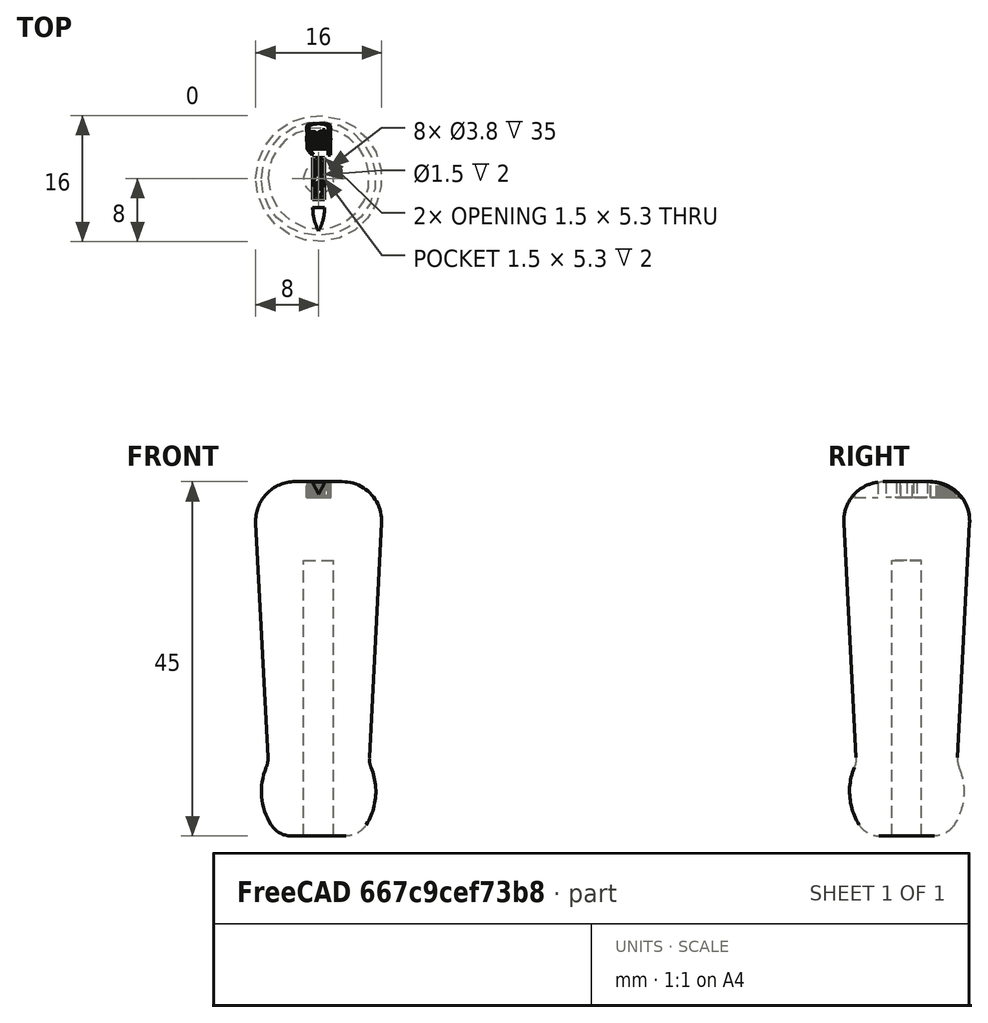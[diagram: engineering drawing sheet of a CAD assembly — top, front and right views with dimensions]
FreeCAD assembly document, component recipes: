
FREECAD ASSEMBLY — COMPONENT RECIPES ("NeedleFileHandle")

This assembly document has 10 components, labeled P0..P9 below (a component is one placed body or linked part). 10 of them carry a construction recipe — the FreeCAD feature program that regenerates the part from scratch, quoted from this document or its linked companion documents; the rest are supplied as boundary geometry only. No exploded tour is included for this assembly.
COMPONENT P0 — recipe-attached ("3 - Dagger Rounded", modeled in this document).
Construction recipe (the document's own serialized feature program — sketch geometry with constraints, then the solid features built on it; lengths are millimeters unless a unit is written):

FEATURE [Sketcher::SketchObject] Sketch004
  ArcFitTolerance = 1e-06
  AttachmentSupport = -> [XZ_Plane005]
  FullyConstrained = true
  MakeInternals = false
  MapMode = 5
  Placement = pos=(0,0,0) rot=(1,0,0;1.5708rad)
  expr: Constraints[10] = <<Spreadsheet>>.TopFlatDiameter / 2
  expr: Constraints[22] = <<Spreadsheet>>.TopRadius
  expr: Constraints[23] = <<Spreadsheet>>.BottomRadius1
  expr: Constraints[24] = <<Spreadsheet>>.BottomRadius2
  expr: Constraints[25] = <<Spreadsheet>>.BottomToStraightHeight
  expr: Constraints[26] = <<Spreadsheet>>.BottomFlatDiameter / 2
  expr: Constraints[27] = <<Spreadsheet>>.BottomRadius3
  expr: Constraints[5] = <<Spreadsheet>>.HoleDiameter / 2
  expr: Constraints[6] = <<Spreadsheet>>.HoleDepth
  expr: Constraints[7] = <<Spreadsheet>>.TopSolidLength
  sketch-geometry (10):
    g0: LineSegment StartX=-1.9 StartY=0 StartZ=0 EndX=-1.9 EndY=35 EndZ=0
    g1: LineSegment StartX=-1.9 StartY=35 StartZ=0 EndX=0 EndY=35 EndZ=0
    g2: LineSegment StartX=0 StartY=35 StartZ=0 EndX=0 EndY=45 EndZ=0
    g3: LineSegment StartX=0 StartY=45 StartZ=0 EndX=-3 EndY=45 EndZ=0
    g4: ArcOfCircle CenterX=-3 CenterY=40 CenterZ=0 NormalX=0 NormalY=0 NormalZ=1 AngleXU=0 Radius=5 StartAngle=1.5708 EndAngle=3.19395
    g5: LineSegment StartX=-1.9 StartY=0 StartZ=0 EndX=-3.5 EndY=0 EndZ=0
    g6: ArcOfCircle CenterX=-3.5 CenterY=3 CenterZ=0 NormalX=0 NormalY=0 NormalZ=1 AngleXU=0 Radius=3 StartAngle=3.70042 EndAngle=4.71239
    g7: ArcOfCircle CenterX=0.739385 CenterY=5.65096 CenterZ=0 NormalX=0 NormalY=0 NormalZ=1 AngleXU=0 Radius=8 StartAngle=2.75061 EndAngle=3.70042
    g8: ArcOfCircle CenterX=-9.43052 CenterY=9.84299 CenterZ=0 NormalX=0 NormalY=0 NormalZ=1 AngleXU=0 Radius=3 StartAngle=5.89221 EndAngle=6.33555
    g9: LineSegment StartX=-6.43463 StartY=10 StartZ=0 EndX=-7.99315 EndY=39.7383 EndZ=0
  constraints (28):
    c: PointOnObject(g0,g-1)
    c: Vertical(g0)
    c: Coincident(g0,g1)
    c: PointOnObject(g1,g-2)
    c: Horizontal(g1)
    c: DistanceX(g1,g1) = 1.9
    c: DistanceY(g0,g0) = 35
    c: Distance(g2) = 10
    c: Coincident(g2,g1)
    c: PointOnObject(g2,g-2)
    c: Distance(g3) = 3
    c: Coincident(g3,g2)
    c: Horizontal(g3)
    c: Coincident(g5,g0)
    c: PointOnObject(g5,g-1)
    c: Tangent(g6,g5) = 1.5708
    c: Tangent(g7,g6) = -1.5708
    c: Tangent(g8,g7) = 1.5708
    c: Tangent(g9,g8) = -1.5708
    c: Tangent(g4,g3) = -1.5708
    c: Tangent(g9,g4) = 1.5708
    c: Angle(g-2,g9) = 0.0523599
    c: Radius(g4) = 5
    c: Radius(g6) = 3
    c: Radius(g7) = 8
    c: DistanceY(g8) = 10
    c: DistanceX(g5,g-1) = 3.5
    c: Radius(g8) = 3
FEATURE [PartDesign::Revolution] Revolution002
  Angle = 360
  Angle2 = 60
  Axis = (0,2e-16,1)
  Base = (0,0,0)
  Placement = pos=(0,0,0) rot=(1,0,0;1.5708rad)
  Profile = -> Sketch004
  ReferenceAxis = -> Sketch004 [V_Axis]
  Refine = true
  Suppressed = false
  Type = 0
FEATURE [Sketcher::SketchObject] Sketch005
  ArcFitTolerance = 1e-06
  AttachmentSupport = -> [Revolution002]
  FullyConstrained = true
  MakeInternals = false
  MapMode = 5
  Placement = pos=(0,1e-14,45) rot=(0,0,1;3.14159rad)
  sketch-geometry (11):
    g0: LineSegment [constr] StartX=-0.75 StartY=-2.65 StartZ=0 EndX=0.75 EndY=-2.65 EndZ=0
    g1: LineSegment [constr] StartX=0.75 StartY=-2.65 StartZ=0 EndX=0.75 EndY=2.65 EndZ=0
    g2: LineSegment [constr] StartX=0.75 StartY=2.65 StartZ=0 EndX=-0.75 EndY=2.65 EndZ=0
    g3: LineSegment [constr] StartX=-0.75 StartY=2.65 StartZ=0 EndX=-0.75 EndY=-2.65 EndZ=0
    g4: GeomPoint [constr] X=0 Y=0 Z=0
    g5: LineSegment StartX=-0.75 StartY=3.65 StartZ=0 EndX=0.75 EndY=3.65 EndZ=0
    g6: ArcOfCircle CenterX=5.625 CenterY=3.65 CenterZ=0 NormalX=0 NormalY=0 NormalZ=1 AngleXU=0 Radius=6.375 StartAngle=2.65164 EndAngle=3.14159
    g7: ArcOfCircle CenterX=-5.625 CenterY=3.65 CenterZ=0 NormalX=0 NormalY=0 NormalZ=1 AngleXU=0 Radius=6.375 StartAngle=0 EndAngle=0.489957
    g8: ArcOfCircle CenterX=4.30667 CenterY=-7e-16 CenterZ=0 NormalX=0 NormalY=0 NormalZ=1 AngleXU=0 Radius=5.05667 StartAngle=2.58998 EndAngle=3.6932
    g9: ArcOfCircle CenterX=-4.30667 CenterY=7e-16 CenterZ=0 NormalX=0 NormalY=0 NormalZ=1 AngleXU=0 Radius=5.05667 StartAngle=5.73157 EndAngle=6.8348
    g10: GeomPoint X=0.75 Y=0 Z=0
  constraints (31):
    c: Coincident(g0,g1)
    c: Coincident(g1,g2)
    c: Coincident(g2,g3)
    c: Coincident(g3,g0)
    c: Horizontal(g0)
    c: Horizontal(g2)
    c: Vertical(g1)
    c: Vertical(g3)
    c: Symmetric(g2,g0,g4)
    c: Distance(g1,g3) = 1.5
    c: Distance(g0,g2) = 5.3
    c: Coincident(g4,g-1)
    c: Horizontal(g5)
    c: Coincident(g6,g5)
    c: PointOnObject(g6,g-2)
    c: Coincident(g7,g6)
    c: Coincident(g7,g5)
    c: Equal(g7,g6)
    c: Equal(g2,g5)
    c: Vertical(g5,g2)
    c: DistanceY(g1,g5) = 1
    c: DistanceY(g5,g6) = 3
    c: Perpendicular(g7,g5)
    c: Symmetric(g2,g2,g8)
    c: Symmetric(g0,g0,g8)
    c: Coincident(g9,g8)
    c: Coincident(g9,g8)
    c: PointOnObject(g10,g1)
    c: PointOnObject(g10,g9)
    c: PointOnObject(g10,g-1)
    c: Equal(g9,g8)
FEATURE [PartDesign::Pocket] Pocket002
  BaseFeature = -> Revolution002
  Direction = (0,0,-1)
  Length = 2
  Length2 = 5
  Placement = pos=(0,0,0) rot=(1,0,0;1.5708rad)
  Profile = -> Sketch005
  ReferenceAxis = -> Sketch005 [N_Axis]
  Refine = true
  Suppressed = false
  Type = 0
FEATURE [PartDesign::Body] Body002
  AllowCompound = false
  Group = -> [Sketch004,Revolution002,Sketch005,Pocket002]
  Origin = -> Origin005
  Tip = -> Pocket002
COMPONENT P1 — recipe-attached ("4 - Dagger Rounded Small", modeled in this document).
Construction recipe (the document's own serialized feature program — sketch geometry with constraints, then the solid features built on it; lengths are millimeters unless a unit is written):

FEATURE [Sketcher::SketchObject] Sketch006
  ArcFitTolerance = 1e-06
  AttachmentSupport = -> [XZ_Plane007]
  FullyConstrained = true
  MakeInternals = false
  MapMode = 5
  Placement = pos=(0,0,0) rot=(1,0,0;1.5708rad)
  expr: Constraints[10] = <<Spreadsheet>>.TopFlatDiameter / 2
  expr: Constraints[22] = <<Spreadsheet>>.TopRadius
  expr: Constraints[23] = <<Spreadsheet>>.BottomRadius1
  expr: Constraints[24] = <<Spreadsheet>>.BottomRadius2
  expr: Constraints[25] = <<Spreadsheet>>.BottomToStraightHeight
  expr: Constraints[26] = <<Spreadsheet>>.BottomFlatDiameter / 2
  expr: Constraints[27] = <<Spreadsheet>>.BottomRadius3
  expr: Constraints[5] = <<Spreadsheet>>.HoleDiameter / 2
  expr: Constraints[6] = <<Spreadsheet>>.HoleDepth
  expr: Constraints[7] = <<Spreadsheet>>.TopSolidLength
  sketch-geometry (10):
    g0: LineSegment StartX=-1.9 StartY=0 StartZ=0 EndX=-1.9 EndY=35 EndZ=0
    g1: LineSegment StartX=-1.9 StartY=35 StartZ=0 EndX=0 EndY=35 EndZ=0
    g2: LineSegment StartX=0 StartY=35 StartZ=0 EndX=0 EndY=45 EndZ=0
    g3: LineSegment StartX=0 StartY=45 StartZ=0 EndX=-3 EndY=45 EndZ=0
    g4: ArcOfCircle CenterX=-3 CenterY=40 CenterZ=0 NormalX=0 NormalY=0 NormalZ=1 AngleXU=0 Radius=5 StartAngle=1.5708 EndAngle=3.19395
    g5: LineSegment StartX=-1.9 StartY=0 StartZ=0 EndX=-3.5 EndY=0 EndZ=0
    g6: ArcOfCircle CenterX=-3.5 CenterY=3 CenterZ=0 NormalX=0 NormalY=0 NormalZ=1 AngleXU=0 Radius=3 StartAngle=3.70042 EndAngle=4.71239
    g7: ArcOfCircle CenterX=0.739385 CenterY=5.65096 CenterZ=0 NormalX=0 NormalY=0 NormalZ=1 AngleXU=0 Radius=8 StartAngle=2.75061 EndAngle=3.70042
    g8: ArcOfCircle CenterX=-9.43052 CenterY=9.84299 CenterZ=0 NormalX=0 NormalY=0 NormalZ=1 AngleXU=0 Radius=3 StartAngle=5.89221 EndAngle=6.33555
    g9: LineSegment StartX=-6.43463 StartY=10 StartZ=0 EndX=-7.99315 EndY=39.7383 EndZ=0
  constraints (28):
    c: PointOnObject(g0,g-1)
    c: Vertical(g0)
    c: Coincident(g0,g1)
    c: PointOnObject(g1,g-2)
    c: Horizontal(g1)
    c: DistanceX(g1,g1) = 1.9
    c: DistanceY(g0,g0) = 35
    c: Distance(g2) = 10
    c: Coincident(g2,g1)
    c: PointOnObject(g2,g-2)
    c: Distance(g3) = 3
    c: Coincident(g3,g2)
    c: Horizontal(g3)
    c: Coincident(g5,g0)
    c: PointOnObject(g5,g-1)
    c: Tangent(g6,g5) = 1.5708
    c: Tangent(g7,g6) = -1.5708
    c: Tangent(g8,g7) = 1.5708
    c: Tangent(g9,g8) = -1.5708
    c: Tangent(g4,g3) = -1.5708
    c: Tangent(g9,g4) = 1.5708
    c: Angle(g-2,g9) = 0.0523599
    c: Radius(g4) = 5
    c: Radius(g6) = 3
    c: Radius(g7) = 8
    c: DistanceY(g8) = 10
    c: DistanceX(g5,g-1) = 3.5
    c: Radius(g8) = 3
FEATURE [PartDesign::Revolution] Revolution003
  Angle = 360
  Angle2 = 60
  Axis = (0,2e-16,1)
  Base = (0,0,0)
  Placement = pos=(0,0,0) rot=(1,0,0;1.5708rad)
  Profile = -> Sketch006
  ReferenceAxis = -> Sketch006 [V_Axis]
  Refine = true
  Suppressed = false
  Type = 0
FEATURE [Sketcher::SketchObject] Sketch007
  ArcFitTolerance = 1e-06
  AttachmentSupport = -> [Revolution003]
  FullyConstrained = true
  MakeInternals = false
  MapMode = 5
  Placement = pos=(0,1e-14,45) rot=(0,0,1;3.14159rad)
  sketch-geometry (13):
    g0: LineSegment [constr] StartX=-0.75 StartY=-2.65 StartZ=0 EndX=0.75 EndY=-2.65 EndZ=0
    g1: LineSegment [constr] StartX=0.75 StartY=-2.65 StartZ=0 EndX=0.75 EndY=2.65 EndZ=0
    g2: LineSegment [constr] StartX=0.75 StartY=2.65 StartZ=0 EndX=-0.75 EndY=2.65 EndZ=0
    g3: LineSegment [constr] StartX=-0.75 StartY=2.65 StartZ=0 EndX=-0.75 EndY=-2.65 EndZ=0
    g4: GeomPoint [constr] X=0 Y=0 Z=0
    g5: LineSegment StartX=-0.75 StartY=3.65 StartZ=0 EndX=0.75 EndY=3.65 EndZ=0
    g6: ArcOfCircle CenterX=5.625 CenterY=3.65 CenterZ=0 NormalX=0 NormalY=0 NormalZ=1 AngleXU=0 Radius=6.375 StartAngle=2.65164 EndAngle=3.14159
    g7: ArcOfCircle CenterX=-5.625 CenterY=3.65 CenterZ=0 NormalX=0 NormalY=0 NormalZ=1 AngleXU=0 Radius=6.375 StartAngle=0 EndAngle=0.489957
    g8: GeomPoint X=0.75 Y=0 Z=0
    g9: ArcOfCircle CenterX=0.795417 CenterY=0 CenterZ=0 NormalX=0 NormalY=0 NormalZ=1 AngleXU=0 Radius=1.54542 StartAngle=2.11145 EndAngle=4.17174
    g10: ArcOfCircle CenterX=-0.795417 CenterY=0 CenterZ=0 NormalX=0 NormalY=0 NormalZ=1 AngleXU=0 Radius=1.54542 StartAngle=5.25304 EndAngle=7.31333
    g11: LineSegment [constr] StartX=1.393e-13 StartY=1.325 StartZ=0 EndX=0 EndY=2.65 EndZ=0
    g12: LineSegment [constr] StartX=1.393e-13 StartY=1.325 StartZ=0 EndX=0 EndY=0 EndZ=0
  constraints (36):
    c: Coincident(g0,g1)
    c: Coincident(g1,g2)
    c: Coincident(g2,g3)
    c: Coincident(g3,g0)
    c: Horizontal(g0)
    c: Horizontal(g2)
    c: Vertical(g1)
    c: Vertical(g3)
    c: Symmetric(g2,g0,g4)
    c: Distance(g1,g3) = 1.5
    c: Distance(g0,g2) = 5.3
    c: Coincident(g4,g-1)
    c: Horizontal(g5)
    c: Coincident(g6,g5)
    c: PointOnObject(g6,g-2)
    c: Coincident(g7,g6)
    c: Coincident(g7,g5)
    c: Equal(g7,g6)
    c: Equal(g2,g5)
    c: Vertical(g5,g2)
    c: DistanceY(g1,g5) = 1
    c: DistanceY(g5,g6) = 3
    c: Perpendicular(g7,g5)
    c: PointOnObject(g8,g1)
    c: PointOnObject(g8,g-1)
    c: PointOnObject(g9,g-2)
    c: Coincident(g10,g9)
    c: Coincident(g10,g9)
    c: PointOnObject(g8,g10)
    c: Symmetric(g9,g9,g4)
    c: Equal(g9,g10)
    c: Coincident(g11,g9)
    c: Symmetric(g2,g2,g11)
    c: Coincident(g12,g9)
    c: Coincident(g12,g4)
    c: Equal(g11,g12)
FEATURE [PartDesign::Pocket] Pocket003
  BaseFeature = -> Revolution003
  Direction = (0,0,-1)
  Length = 2
  Length2 = 5
  Placement = pos=(0,0,0) rot=(1,0,0;1.5708rad)
  Profile = -> Sketch007
  ReferenceAxis = -> Sketch007 [N_Axis]
  Refine = true
  Suppressed = false
  Type = 0
FEATURE [PartDesign::Body] Body003
  AllowCompound = false
  Group = -> [Sketch006,Revolution003,Sketch007,Pocket003]
  Origin = -> Origin007
  Tip = -> Pocket003
COMPONENT P2 — recipe-attached ("5 - Triangle Flattened", modeled in this document).
Construction recipe (the document's own serialized feature program — sketch geometry with constraints, then the solid features built on it; lengths are millimeters unless a unit is written):

FEATURE [Sketcher::SketchObject] Sketch008
  ArcFitTolerance = 1e-06
  AttachmentSupport = -> [XZ_Plane009]
  FullyConstrained = true
  MakeInternals = false
  MapMode = 5
  Placement = pos=(0,0,0) rot=(1,0,0;1.5708rad)
  expr: Constraints[10] = <<Spreadsheet>>.TopFlatDiameter / 2
  expr: Constraints[22] = <<Spreadsheet>>.TopRadius
  expr: Constraints[23] = <<Spreadsheet>>.BottomRadius1
  expr: Constraints[24] = <<Spreadsheet>>.BottomRadius2
  expr: Constraints[25] = <<Spreadsheet>>.BottomToStraightHeight
  expr: Constraints[26] = <<Spreadsheet>>.BottomFlatDiameter / 2
  expr: Constraints[27] = <<Spreadsheet>>.BottomRadius3
  expr: Constraints[5] = <<Spreadsheet>>.HoleDiameter / 2
  expr: Constraints[6] = <<Spreadsheet>>.HoleDepth
  expr: Constraints[7] = <<Spreadsheet>>.TopSolidLength
  sketch-geometry (10):
    g0: LineSegment StartX=-1.9 StartY=0 StartZ=0 EndX=-1.9 EndY=35 EndZ=0
    g1: LineSegment StartX=-1.9 StartY=35 StartZ=0 EndX=0 EndY=35 EndZ=0
    g2: LineSegment StartX=0 StartY=35 StartZ=0 EndX=0 EndY=45 EndZ=0
    g3: LineSegment StartX=0 StartY=45 StartZ=0 EndX=-3 EndY=45 EndZ=0
    g4: ArcOfCircle CenterX=-3 CenterY=40 CenterZ=0 NormalX=0 NormalY=0 NormalZ=1 AngleXU=0 Radius=5 StartAngle=1.5708 EndAngle=3.19395
    g5: LineSegment StartX=-1.9 StartY=0 StartZ=0 EndX=-3.5 EndY=0 EndZ=0
    g6: ArcOfCircle CenterX=-3.5 CenterY=3 CenterZ=0 NormalX=0 NormalY=0 NormalZ=1 AngleXU=0 Radius=3 StartAngle=3.70042 EndAngle=4.71239
    g7: ArcOfCircle CenterX=0.739385 CenterY=5.65096 CenterZ=0 NormalX=0 NormalY=0 NormalZ=1 AngleXU=0 Radius=8 StartAngle=2.75061 EndAngle=3.70042
    g8: ArcOfCircle CenterX=-9.43052 CenterY=9.84299 CenterZ=0 NormalX=0 NormalY=0 NormalZ=1 AngleXU=0 Radius=3 StartAngle=5.89221 EndAngle=6.33555
    g9: LineSegment StartX=-6.43463 StartY=10 StartZ=0 EndX=-7.99315 EndY=39.7383 EndZ=0
  constraints (28):
    c: PointOnObject(g0,g-1)
    c: Vertical(g0)
    c: Coincident(g0,g1)
    c: PointOnObject(g1,g-2)
    c: Horizontal(g1)
    c: DistanceX(g1,g1) = 1.9
    c: DistanceY(g0,g0) = 35
    c: Distance(g2) = 10
    c: Coincident(g2,g1)
    c: PointOnObject(g2,g-2)
    c: Distance(g3) = 3
    c: Coincident(g3,g2)
    c: Horizontal(g3)
    c: Coincident(g5,g0)
    c: PointOnObject(g5,g-1)
    c: Tangent(g6,g5) = 1.5708
    c: Tangent(g7,g6) = -1.5708
    c: Tangent(g8,g7) = 1.5708
    c: Tangent(g9,g8) = -1.5708
    c: Tangent(g4,g3) = -1.5708
    c: Tangent(g9,g4) = 1.5708
    c: Angle(g-2,g9) = 0.0523599
    c: Radius(g4) = 5
    c: Radius(g6) = 3
    c: Radius(g7) = 8
    c: DistanceY(g8) = 10
    c: DistanceX(g5,g-1) = 3.5
    c: Radius(g8) = 3
FEATURE [PartDesign::Revolution] Revolution004
  Angle = 360
  Angle2 = 60
  Axis = (0,2e-16,1)
  Base = (0,0,0)
  Placement = pos=(0,0,0) rot=(1,0,0;1.5708rad)
  Profile = -> Sketch008
  ReferenceAxis = -> Sketch008 [V_Axis]
  Refine = true
  Suppressed = false
  Type = 0
FEATURE [Sketcher::SketchObject] Sketch009
  ArcFitTolerance = 1e-06
  AttachmentSupport = -> [Revolution004]
  FullyConstrained = true
  MakeInternals = false
  MapMode = 5
  Placement = pos=(0,1e-14,45) rot=(0,0,1;3.14159rad)
  sketch-geometry (12):
    g0: LineSegment [constr] StartX=-0.75 StartY=-2.65 StartZ=0 EndX=0.75 EndY=-2.65 EndZ=0
    g1: LineSegment [constr] StartX=0.75 StartY=-2.65 StartZ=0 EndX=0.75 EndY=2.65 EndZ=0
    g2: LineSegment [constr] StartX=0.75 StartY=2.65 StartZ=0 EndX=-0.75 EndY=2.65 EndZ=0
    g3: LineSegment [constr] StartX=-0.75 StartY=2.65 StartZ=0 EndX=-0.75 EndY=-2.65 EndZ=0
    g4: GeomPoint [constr] X=0 Y=0 Z=0
    g5: LineSegment StartX=-0.75 StartY=3.65 StartZ=0 EndX=0.75 EndY=3.65 EndZ=0
    g6: ArcOfCircle CenterX=5.625 CenterY=3.65 CenterZ=0 NormalX=0 NormalY=0 NormalZ=1 AngleXU=0 Radius=6.375 StartAngle=2.65164 EndAngle=3.14159
    g7: ArcOfCircle CenterX=-5.625 CenterY=3.65 CenterZ=0 NormalX=0 NormalY=0 NormalZ=1 AngleXU=0 Radius=6.375 StartAngle=1e-16 EndAngle=0.489957
    g8: GeomPoint X=0.75 Y=0 Z=0
    g9: LineSegment StartX=0.75 StartY=2.65 StartZ=0 EndX=0.75 EndY=-2.65 EndZ=0
    g10: LineSegment StartX=0.75 StartY=-2.65 StartZ=0 EndX=-0.75 EndY=0 EndZ=0
    g11: LineSegment StartX=-0.75 StartY=0 StartZ=0 EndX=0.75 EndY=2.65 EndZ=0
  constraints (31):
    c: Coincident(g0,g1)
    c: Coincident(g1,g2)
    c: Coincident(g2,g3)
    c: Coincident(g3,g0)
    c: Horizontal(g0)
    c: Horizontal(g2)
    c: Vertical(g1)
    c: Vertical(g3)
    c: Symmetric(g2,g0,g4)
    c: Distance(g1,g3) = 1.5
    c: Distance(g0,g2) = 5.3
    c: Coincident(g4,g-1)
    c: Horizontal(g5)
    c: Coincident(g6,g5)
    c: PointOnObject(g6,g-2)
    c: Coincident(g7,g6)
    c: Coincident(g7,g5)
    c: Equal(g7,g6)
    c: Equal(g2,g5)
    c: Vertical(g5,g2)
    c: DistanceY(g1,g5) = 1
    c: DistanceY(g5,g6) = 3
    c: Perpendicular(g7,g5)
    c: PointOnObject(g8,g1)
    c: PointOnObject(g8,g-1)
    c: Coincident(g9,g10)
    c: Symmetric(g3,g3,g10)
    c: Coincident(g10,g11)
    c: Coincident(g11,g9)
    c: Coincident(g9,g0)
    c: Coincident(g9,g1)
FEATURE [PartDesign::Pocket] Pocket004
  BaseFeature = -> Revolution004
  Direction = (0,0,-1)
  Length = 2
  Length2 = 5
  Placement = pos=(0,0,0) rot=(1,0,0;1.5708rad)
  Profile = -> Sketch009
  ReferenceAxis = -> Sketch009 [N_Axis]
  Refine = true
  Suppressed = false
  Type = 0
FEATURE [PartDesign::Body] Body004
  AllowCompound = false
  Group = -> [Sketch008,Revolution004,Sketch009,Pocket004]
  Origin = -> Origin009
  Tip = -> Pocket004
COMPONENT P3 — recipe-attached ("6 - Knife", modeled in this document).
Construction recipe (the document's own serialized feature program — sketch geometry with constraints, then the solid features built on it; lengths are millimeters unless a unit is written):

FEATURE [Sketcher::SketchObject] Sketch010
  ArcFitTolerance = 1e-06
  AttachmentSupport = -> [XZ_Plane011]
  FullyConstrained = true
  MakeInternals = false
  MapMode = 5
  Placement = pos=(0,0,0) rot=(1,0,0;1.5708rad)
  expr: Constraints[10] = <<Spreadsheet>>.TopFlatDiameter / 2
  expr: Constraints[22] = <<Spreadsheet>>.TopRadius
  expr: Constraints[23] = <<Spreadsheet>>.BottomRadius1
  expr: Constraints[24] = <<Spreadsheet>>.BottomRadius2
  expr: Constraints[25] = <<Spreadsheet>>.BottomToStraightHeight
  expr: Constraints[26] = <<Spreadsheet>>.BottomFlatDiameter / 2
  expr: Constraints[27] = <<Spreadsheet>>.BottomRadius3
  expr: Constraints[5] = <<Spreadsheet>>.HoleDiameter / 2
  expr: Constraints[6] = <<Spreadsheet>>.HoleDepth
  expr: Constraints[7] = <<Spreadsheet>>.TopSolidLength
  sketch-geometry (10):
    g0: LineSegment StartX=-1.9 StartY=0 StartZ=0 EndX=-1.9 EndY=35 EndZ=0
    g1: LineSegment StartX=-1.9 StartY=35 StartZ=0 EndX=0 EndY=35 EndZ=0
    g2: LineSegment StartX=0 StartY=35 StartZ=0 EndX=0 EndY=45 EndZ=0
    g3: LineSegment StartX=0 StartY=45 StartZ=0 EndX=-3 EndY=45 EndZ=0
    g4: ArcOfCircle CenterX=-3 CenterY=40 CenterZ=0 NormalX=0 NormalY=0 NormalZ=1 AngleXU=0 Radius=5 StartAngle=1.5708 EndAngle=3.19395
    g5: LineSegment StartX=-1.9 StartY=0 StartZ=0 EndX=-3.5 EndY=0 EndZ=0
    g6: ArcOfCircle CenterX=-3.5 CenterY=3 CenterZ=0 NormalX=0 NormalY=0 NormalZ=1 AngleXU=0 Radius=3 StartAngle=3.70042 EndAngle=4.71239
    g7: ArcOfCircle CenterX=0.739385 CenterY=5.65096 CenterZ=0 NormalX=0 NormalY=0 NormalZ=1 AngleXU=0 Radius=8 StartAngle=2.75061 EndAngle=3.70042
    g8: ArcOfCircle CenterX=-9.43052 CenterY=9.84299 CenterZ=0 NormalX=0 NormalY=0 NormalZ=1 AngleXU=0 Radius=3 StartAngle=5.89221 EndAngle=6.33555
    g9: LineSegment StartX=-6.43463 StartY=10 StartZ=0 EndX=-7.99315 EndY=39.7383 EndZ=0
  constraints (28):
    c: PointOnObject(g0,g-1)
    c: Vertical(g0)
    c: Coincident(g0,g1)
    c: PointOnObject(g1,g-2)
    c: Horizontal(g1)
    c: DistanceX(g1,g1) = 1.9
    c: DistanceY(g0,g0) = 35
    c: Distance(g2) = 10
    c: Coincident(g2,g1)
    c: PointOnObject(g2,g-2)
    c: Distance(g3) = 3
    c: Coincident(g3,g2)
    c: Horizontal(g3)
    c: Coincident(g5,g0)
    c: PointOnObject(g5,g-1)
    c: Tangent(g6,g5) = 1.5708
    c: Tangent(g7,g6) = -1.5708
    c: Tangent(g8,g7) = 1.5708
    c: Tangent(g9,g8) = -1.5708
    c: Tangent(g4,g3) = -1.5708
    c: Tangent(g9,g4) = 1.5708
    c: Angle(g-2,g9) = 0.0523599
    c: Radius(g4) = 5
    c: Radius(g6) = 3
    c: Radius(g7) = 8
    c: DistanceY(g8) = 10
    c: DistanceX(g5,g-1) = 3.5
    c: Radius(g8) = 3
FEATURE [PartDesign::Revolution] Revolution005
  Angle = 360
  Angle2 = 60
  Axis = (0,2e-16,1)
  Base = (0,0,0)
  Placement = pos=(0,0,0) rot=(1,0,0;1.5708rad)
  Profile = -> Sketch010
  ReferenceAxis = -> Sketch010 [V_Axis]
  Refine = true
  Suppressed = false
  Type = 0
FEATURE [Sketcher::SketchObject] Sketch011
  ArcFitTolerance = 1e-06
  AttachmentSupport = -> [Revolution005]
  FullyConstrained = true
  MakeInternals = false
  MapMode = 5
  Placement = pos=(0,1e-14,45) rot=(0,0,1;3.14159rad)
  sketch-geometry (12):
    g0: LineSegment [constr] StartX=-0.75 StartY=-2.65 StartZ=0 EndX=0.75 EndY=-2.65 EndZ=0
    g1: LineSegment [constr] StartX=0.75 StartY=-2.65 StartZ=0 EndX=0.75 EndY=2.65 EndZ=0
    g2: LineSegment [constr] StartX=0.75 StartY=2.65 StartZ=0 EndX=-0.75 EndY=2.65 EndZ=0
    g3: LineSegment [constr] StartX=-0.75 StartY=2.65 StartZ=0 EndX=-0.75 EndY=-2.65 EndZ=0
    g4: GeomPoint [constr] X=0 Y=0 Z=0
    g5: LineSegment StartX=-0.75 StartY=3.65 StartZ=0 EndX=0.75 EndY=3.65 EndZ=0
    g6: ArcOfCircle CenterX=5.625 CenterY=3.65 CenterZ=0 NormalX=0 NormalY=0 NormalZ=1 AngleXU=0 Radius=6.375 StartAngle=2.65164 EndAngle=3.14159
    g7: ArcOfCircle CenterX=-5.625 CenterY=3.65 CenterZ=0 NormalX=0 NormalY=0 NormalZ=1 AngleXU=0 Radius=6.375 StartAngle=0 EndAngle=0.489957
    g8: GeomPoint X=0.75 Y=0 Z=0
    g9: LineSegment StartX=-0.75 StartY=1.325 StartZ=0 EndX=0.75 EndY=1.325 EndZ=0
    g10: LineSegment StartX=0.75 StartY=1.325 StartZ=0 EndX=0 EndY=-2.65 EndZ=0
    g11: LineSegment StartX=0 StartY=-2.65 StartZ=0 EndX=-0.75 EndY=1.325 EndZ=0
  constraints (32):
    c: Coincident(g0,g1)
    c: Coincident(g1,g2)
    c: Coincident(g2,g3)
    c: Coincident(g3,g0)
    c: Horizontal(g0)
    c: Horizontal(g2)
    c: Vertical(g1)
    c: Vertical(g3)
    c: Symmetric(g2,g0,g4)
    c: Distance(g1,g3) = 1.5
    c: Distance(g0,g2) = 5.3
    c: Coincident(g4,g-1)
    c: Horizontal(g5)
    c: Coincident(g6,g5)
    c: PointOnObject(g6,g-2)
    c: Coincident(g7,g6)
    c: Coincident(g7,g5)
    c: Equal(g7,g6)
    c: Equal(g2,g5)
    c: Vertical(g5,g2)
    c: DistanceY(g1,g5) = 1
    c: DistanceY(g5,g6) = 3
    c: Perpendicular(g7,g5)
    c: PointOnObject(g8,g1)
    c: PointOnObject(g8,g-1)
    c: PointOnObject(g9,g3)
    c: Horizontal(g9)
    c: Coincident(g9,g10)
    c: Symmetric(g0,g0,g10)
    c: Coincident(g10,g11)
    c: Coincident(g11,g9)
    c: Symmetric(g8,g1,g9)
FEATURE [PartDesign::Pocket] Pocket005
  BaseFeature = -> Revolution005
  Direction = (0,0,-1)
  Length = 2
  Length2 = 5
  Placement = pos=(0,0,0) rot=(1,0,0;1.5708rad)
  Profile = -> Sketch011
  ReferenceAxis = -> Sketch011 [N_Axis]
  Refine = true
  Suppressed = false
  Type = 0
FEATURE [PartDesign::Body] Body005
  AllowCompound = false
  Group = -> [Sketch010,Revolution005,Sketch011,Pocket005]
  Origin = -> Origin011
  Tip = -> Pocket005
COMPONENT P4 — recipe-attached ("7 - Round", modeled in this document).
Construction recipe (the document's own serialized feature program — sketch geometry with constraints, then the solid features built on it; lengths are millimeters unless a unit is written):

FEATURE [Sketcher::SketchObject] Sketch012
  ArcFitTolerance = 1e-06
  AttachmentSupport = -> [XZ_Plane013]
  FullyConstrained = true
  MakeInternals = false
  MapMode = 5
  Placement = pos=(0,0,0) rot=(1,0,0;1.5708rad)
  expr: Constraints[10] = <<Spreadsheet>>.TopFlatDiameter / 2
  expr: Constraints[22] = <<Spreadsheet>>.TopRadius
  expr: Constraints[23] = <<Spreadsheet>>.BottomRadius1
  expr: Constraints[24] = <<Spreadsheet>>.BottomRadius2
  expr: Constraints[25] = <<Spreadsheet>>.BottomToStraightHeight
  expr: Constraints[26] = <<Spreadsheet>>.BottomFlatDiameter / 2
  expr: Constraints[27] = <<Spreadsheet>>.BottomRadius3
  expr: Constraints[5] = <<Spreadsheet>>.HoleDiameter / 2
  expr: Constraints[6] = <<Spreadsheet>>.HoleDepth
  expr: Constraints[7] = <<Spreadsheet>>.TopSolidLength
  sketch-geometry (10):
    g0: LineSegment StartX=-1.9 StartY=0 StartZ=0 EndX=-1.9 EndY=35 EndZ=0
    g1: LineSegment StartX=-1.9 StartY=35 StartZ=0 EndX=0 EndY=35 EndZ=0
    g2: LineSegment StartX=0 StartY=35 StartZ=0 EndX=0 EndY=45 EndZ=0
    g3: LineSegment StartX=0 StartY=45 StartZ=0 EndX=-3 EndY=45 EndZ=0
    g4: ArcOfCircle CenterX=-3 CenterY=40 CenterZ=0 NormalX=0 NormalY=0 NormalZ=1 AngleXU=0 Radius=5 StartAngle=1.5708 EndAngle=3.19395
    g5: LineSegment StartX=-1.9 StartY=0 StartZ=0 EndX=-3.5 EndY=0 EndZ=0
    g6: ArcOfCircle CenterX=-3.5 CenterY=3 CenterZ=0 NormalX=0 NormalY=0 NormalZ=1 AngleXU=0 Radius=3 StartAngle=3.70042 EndAngle=4.71239
    g7: ArcOfCircle CenterX=0.739385 CenterY=5.65096 CenterZ=0 NormalX=0 NormalY=0 NormalZ=1 AngleXU=0 Radius=8 StartAngle=2.75061 EndAngle=3.70042
    g8: ArcOfCircle CenterX=-9.43052 CenterY=9.84299 CenterZ=0 NormalX=0 NormalY=0 NormalZ=1 AngleXU=0 Radius=3 StartAngle=5.89221 EndAngle=6.33555
    g9: LineSegment StartX=-6.43463 StartY=10 StartZ=0 EndX=-7.99315 EndY=39.7383 EndZ=0
  constraints (28):
    c: PointOnObject(g0,g-1)
    c: Vertical(g0)
    c: Coincident(g0,g1)
    c: PointOnObject(g1,g-2)
    c: Horizontal(g1)
    c: DistanceX(g1,g1) = 1.9
    c: DistanceY(g0,g0) = 35
    c: Distance(g2) = 10
    c: Coincident(g2,g1)
    c: PointOnObject(g2,g-2)
    c: Distance(g3) = 3
    c: Coincident(g3,g2)
    c: Horizontal(g3)
    c: Coincident(g5,g0)
    c: PointOnObject(g5,g-1)
    c: Tangent(g6,g5) = 1.5708
    c: Tangent(g7,g6) = -1.5708
    c: Tangent(g8,g7) = 1.5708
    c: Tangent(g9,g8) = -1.5708
    c: Tangent(g4,g3) = -1.5708
    c: Tangent(g9,g4) = 1.5708
    c: Angle(g-2,g9) = 0.0523599
    c: Radius(g4) = 5
    c: Radius(g6) = 3
    c: Radius(g7) = 8
    c: DistanceY(g8) = 10
    c: DistanceX(g5,g-1) = 3.5
    c: Radius(g8) = 3
FEATURE [PartDesign::Revolution] Revolution006
  Angle = 360
  Angle2 = 60
  Axis = (0,2e-16,1)
  Base = (0,0,0)
  Placement = pos=(0,0,0) rot=(1,0,0;1.5708rad)
  Profile = -> Sketch012
  ReferenceAxis = -> Sketch012 [V_Axis]
  Refine = true
  Suppressed = false
  Type = 0
FEATURE [Sketcher::SketchObject] Sketch013
  ArcFitTolerance = 1e-06
  AttachmentSupport = -> [Revolution006]
  FullyConstrained = true
  MakeInternals = false
  MapMode = 5
  Placement = pos=(0,1e-14,45) rot=(0,0,1;3.14159rad)
  sketch-geometry (10):
    g0: LineSegment [constr] StartX=-0.75 StartY=-2.65 StartZ=0 EndX=0.75 EndY=-2.65 EndZ=0
    g1: LineSegment [constr] StartX=0.75 StartY=-2.65 StartZ=0 EndX=0.75 EndY=2.65 EndZ=0
    g2: LineSegment [constr] StartX=0.75 StartY=2.65 StartZ=0 EndX=-0.75 EndY=2.65 EndZ=0
    g3: LineSegment [constr] StartX=-0.75 StartY=2.65 StartZ=0 EndX=-0.75 EndY=-2.65 EndZ=0
    g4: GeomPoint [constr] X=0 Y=0 Z=0
    g5: LineSegment StartX=-0.75 StartY=3.65 StartZ=0 EndX=0.75 EndY=3.65 EndZ=0
    g6: ArcOfCircle CenterX=5.625 CenterY=3.65 CenterZ=0 NormalX=0 NormalY=0 NormalZ=1 AngleXU=0 Radius=6.375 StartAngle=2.65164 EndAngle=3.14159
    g7: ArcOfCircle CenterX=-5.625 CenterY=3.65 CenterZ=0 NormalX=0 NormalY=0 NormalZ=1 AngleXU=0 Radius=6.375 StartAngle=0 EndAngle=0.489957
    g8: GeomPoint X=0.75 Y=0 Z=0
    g9: Circle CenterX=0 CenterY=0 CenterZ=0 NormalX=0 NormalY=0 NormalZ=1 AngleXU=0 Radius=0.75
  constraints (27):
    c: Coincident(g0,g1)
    c: Coincident(g1,g2)
    c: Coincident(g2,g3)
    c: Coincident(g3,g0)
    c: Horizontal(g0)
    c: Horizontal(g2)
    c: Vertical(g1)
    c: Vertical(g3)
    c: Symmetric(g2,g0,g4)
    c: Distance(g1,g3) = 1.5
    c: Distance(g0,g2) = 5.3
    c: Coincident(g4,g-1)
    c: Horizontal(g5)
    c: Coincident(g6,g5)
    c: PointOnObject(g6,g-2)
    c: Coincident(g7,g6)
    c: Coincident(g7,g5)
    c: Equal(g7,g6)
    c: Equal(g2,g5)
    c: Vertical(g5,g2)
    c: DistanceY(g1,g5) = 1
    c: DistanceY(g5,g6) = 3
    c: Perpendicular(g7,g5)
    c: PointOnObject(g8,g1)
    c: PointOnObject(g8,g-1)
    c: Coincident(g9,g4)
    c: PointOnObject(g8,g9)
FEATURE [PartDesign::Pocket] Pocket006
  BaseFeature = -> Revolution006
  Direction = (0,0,-1)
  Length = 2
  Length2 = 5
  Placement = pos=(0,0,0) rot=(1,0,0;1.5708rad)
  Profile = -> Sketch013
  ReferenceAxis = -> Sketch013 [N_Axis]
  Refine = true
  Suppressed = false
  Type = 0
FEATURE [PartDesign::Body] Body006
  AllowCompound = false
  Group = -> [Sketch012,Revolution006,Sketch013,Pocket006]
  Origin = -> Origin013
  Tip = -> Pocket006
COMPONENT P5 — recipe-attached ("8 - Triangle", modeled in this document).
Construction recipe (the document's own serialized feature program — sketch geometry with constraints, then the solid features built on it; lengths are millimeters unless a unit is written):

FEATURE [Sketcher::SketchObject] Sketch014
  ArcFitTolerance = 1e-06
  AttachmentSupport = -> [XZ_Plane015]
  FullyConstrained = true
  MakeInternals = false
  MapMode = 5
  Placement = pos=(0,0,0) rot=(1,0,0;1.5708rad)
  expr: Constraints[10] = <<Spreadsheet>>.TopFlatDiameter / 2
  expr: Constraints[22] = <<Spreadsheet>>.TopRadius
  expr: Constraints[23] = <<Spreadsheet>>.BottomRadius1
  expr: Constraints[24] = <<Spreadsheet>>.BottomRadius2
  expr: Constraints[25] = <<Spreadsheet>>.BottomToStraightHeight
  expr: Constraints[26] = <<Spreadsheet>>.BottomFlatDiameter / 2
  expr: Constraints[27] = <<Spreadsheet>>.BottomRadius3
  expr: Constraints[5] = <<Spreadsheet>>.HoleDiameter / 2
  expr: Constraints[6] = <<Spreadsheet>>.HoleDepth
  expr: Constraints[7] = <<Spreadsheet>>.TopSolidLength
  sketch-geometry (10):
    g0: LineSegment StartX=-1.9 StartY=0 StartZ=0 EndX=-1.9 EndY=35 EndZ=0
    g1: LineSegment StartX=-1.9 StartY=35 StartZ=0 EndX=0 EndY=35 EndZ=0
    g2: LineSegment StartX=0 StartY=35 StartZ=0 EndX=0 EndY=45 EndZ=0
    g3: LineSegment StartX=0 StartY=45 StartZ=0 EndX=-3 EndY=45 EndZ=0
    g4: ArcOfCircle CenterX=-3 CenterY=40 CenterZ=0 NormalX=0 NormalY=0 NormalZ=1 AngleXU=0 Radius=5 StartAngle=1.5708 EndAngle=3.19395
    g5: LineSegment StartX=-1.9 StartY=0 StartZ=0 EndX=-3.5 EndY=0 EndZ=0
    g6: ArcOfCircle CenterX=-3.5 CenterY=3 CenterZ=0 NormalX=0 NormalY=0 NormalZ=1 AngleXU=0 Radius=3 StartAngle=3.70042 EndAngle=4.71239
    g7: ArcOfCircle CenterX=0.739385 CenterY=5.65096 CenterZ=0 NormalX=0 NormalY=0 NormalZ=1 AngleXU=0 Radius=8 StartAngle=2.75061 EndAngle=3.70042
    g8: ArcOfCircle CenterX=-9.43052 CenterY=9.84299 CenterZ=0 NormalX=0 NormalY=0 NormalZ=1 AngleXU=0 Radius=3 StartAngle=5.89221 EndAngle=6.33555
    g9: LineSegment StartX=-6.43463 StartY=10 StartZ=0 EndX=-7.99315 EndY=39.7383 EndZ=0
  constraints (28):
    c: PointOnObject(g0,g-1)
    c: Vertical(g0)
    c: Coincident(g0,g1)
    c: PointOnObject(g1,g-2)
    c: Horizontal(g1)
    c: DistanceX(g1,g1) = 1.9
    c: DistanceY(g0,g0) = 35
    c: Distance(g2) = 10
    c: Coincident(g2,g1)
    c: PointOnObject(g2,g-2)
    c: Distance(g3) = 3
    c: Coincident(g3,g2)
    c: Horizontal(g3)
    c: Coincident(g5,g0)
    c: PointOnObject(g5,g-1)
    c: Tangent(g6,g5) = 1.5708
    c: Tangent(g7,g6) = -1.5708
    c: Tangent(g8,g7) = 1.5708
    c: Tangent(g9,g8) = -1.5708
    c: Tangent(g4,g3) = -1.5708
    c: Tangent(g9,g4) = 1.5708
    c: Angle(g-2,g9) = 0.0523599
    c: Radius(g4) = 5
    c: Radius(g6) = 3
    c: Radius(g7) = 8
    c: DistanceY(g8) = 10
    c: DistanceX(g5,g-1) = 3.5
    c: Radius(g8) = 3
FEATURE [PartDesign::Revolution] Revolution007
  Angle = 360
  Angle2 = 60
  Axis = (0,2e-16,1)
  Base = (0,0,0)
  Placement = pos=(0,0,0) rot=(1,0,0;1.5708rad)
  Profile = -> Sketch014
  ReferenceAxis = -> Sketch014 [V_Axis]
  Refine = true
  Suppressed = false
  Type = 0
FEATURE [Sketcher::SketchObject] Sketch015
  ArcFitTolerance = 1e-06
  AttachmentSupport = -> [Revolution007]
  FullyConstrained = true
  MakeInternals = false
  MapMode = 5
  Placement = pos=(0,1e-14,45) rot=(0,0,1;3.14159rad)
  sketch-geometry (12):
    g0: LineSegment [constr] StartX=-0.75 StartY=-2.65 StartZ=0 EndX=0.75 EndY=-2.65 EndZ=0
    g1: LineSegment [constr] StartX=0.75 StartY=-2.65 StartZ=0 EndX=0.75 EndY=2.65 EndZ=0
    g2: LineSegment [constr] StartX=0.75 StartY=2.65 StartZ=0 EndX=-0.75 EndY=2.65 EndZ=0
    g3: LineSegment [constr] StartX=-0.75 StartY=2.65 StartZ=0 EndX=-0.75 EndY=-2.65 EndZ=0
    g4: GeomPoint [constr] X=0 Y=0 Z=0
    g5: LineSegment StartX=-0.75 StartY=3.65 StartZ=0 EndX=0.75 EndY=3.65 EndZ=0
    g6: ArcOfCircle CenterX=5.625 CenterY=3.65 CenterZ=0 NormalX=0 NormalY=0 NormalZ=1 AngleXU=0 Radius=6.375 StartAngle=2.65164 EndAngle=3.14159
    g7: ArcOfCircle CenterX=-5.625 CenterY=3.65 CenterZ=0 NormalX=0 NormalY=0 NormalZ=1 AngleXU=0 Radius=6.375 StartAngle=0 EndAngle=0.489957
    g8: GeomPoint X=0.75 Y=0 Z=0
    g9: LineSegment StartX=-0.75 StartY=1e-16 StartZ=0 EndX=0.75 EndY=0.866025 EndZ=0
    g10: LineSegment StartX=0.75 StartY=0.866025 StartZ=0 EndX=0.75 EndY=-0.866025 EndZ=0
    g11: LineSegment StartX=0.75 StartY=-0.866025 StartZ=0 EndX=-0.75 EndY=1e-16 EndZ=0
  constraints (33):
    c: Coincident(g0,g1)
    c: Coincident(g1,g2)
    c: Coincident(g2,g3)
    c: Coincident(g3,g0)
    c: Horizontal(g0)
    c: Horizontal(g2)
    c: Vertical(g1)
    c: Vertical(g3)
    c: Symmetric(g2,g0,g4)
    c: Distance(g1,g3) = 1.5
    c: Distance(g0,g2) = 5.3
    c: Coincident(g4,g-1)
    c: Horizontal(g5)
    c: Coincident(g6,g5)
    c: PointOnObject(g6,g-2)
    c: Coincident(g7,g6)
    c: Coincident(g7,g5)
    c: Equal(g7,g6)
    c: Equal(g2,g5)
    c: Vertical(g5,g2)
    c: DistanceY(g1,g5) = 1
    c: DistanceY(g5,g6) = 3
    c: Perpendicular(g7,g5)
    c: PointOnObject(g8,g1)
    c: PointOnObject(g8,g-1)
    c: Symmetric(g3,g3,g9)
    c: PointOnObject(g9,g1)
    c: Coincident(g9,g10)
    c: PointOnObject(g10,g1)
    c: Coincident(g10,g11)
    c: Coincident(g11,g9)
    c: Equal(g9,g10)
    c: Equal(g10,g11)
FEATURE [PartDesign::Pocket] Pocket007
  BaseFeature = -> Revolution007
  Direction = (0,0,-1)
  Length = 2
  Length2 = 5
  Placement = pos=(0,0,0) rot=(1,0,0;1.5708rad)
  Profile = -> Sketch015
  ReferenceAxis = -> Sketch015 [N_Axis]
  Refine = true
  Suppressed = false
  Type = 0
FEATURE [PartDesign::Body] Body007
  AllowCompound = false
  Group = -> [Sketch014,Revolution007,Sketch015,Pocket007]
  Origin = -> Origin015
  Tip = -> Pocket007
COMPONENT P6 — recipe-attached ("9 - Square", modeled in this document).
Construction recipe (the document's own serialized feature program — sketch geometry with constraints, then the solid features built on it; lengths are millimeters unless a unit is written):

FEATURE [Sketcher::SketchObject] Sketch016
  ArcFitTolerance = 1e-06
  AttachmentSupport = -> [XZ_Plane017]
  FullyConstrained = true
  MakeInternals = false
  MapMode = 5
  Placement = pos=(0,0,0) rot=(1,0,0;1.5708rad)
  expr: Constraints[10] = <<Spreadsheet>>.TopFlatDiameter / 2
  expr: Constraints[22] = <<Spreadsheet>>.TopRadius
  expr: Constraints[23] = <<Spreadsheet>>.BottomRadius1
  expr: Constraints[24] = <<Spreadsheet>>.BottomRadius2
  expr: Constraints[25] = <<Spreadsheet>>.BottomToStraightHeight
  expr: Constraints[26] = <<Spreadsheet>>.BottomFlatDiameter / 2
  expr: Constraints[27] = <<Spreadsheet>>.BottomRadius3
  expr: Constraints[5] = <<Spreadsheet>>.HoleDiameter / 2
  expr: Constraints[6] = <<Spreadsheet>>.HoleDepth
  expr: Constraints[7] = <<Spreadsheet>>.TopSolidLength
  sketch-geometry (10):
    g0: LineSegment StartX=-1.9 StartY=0 StartZ=0 EndX=-1.9 EndY=35 EndZ=0
    g1: LineSegment StartX=-1.9 StartY=35 StartZ=0 EndX=0 EndY=35 EndZ=0
    g2: LineSegment StartX=0 StartY=35 StartZ=0 EndX=0 EndY=45 EndZ=0
    g3: LineSegment StartX=0 StartY=45 StartZ=0 EndX=-3 EndY=45 EndZ=0
    g4: ArcOfCircle CenterX=-3 CenterY=40 CenterZ=0 NormalX=0 NormalY=0 NormalZ=1 AngleXU=0 Radius=5 StartAngle=1.5708 EndAngle=3.19395
    g5: LineSegment StartX=-1.9 StartY=0 StartZ=0 EndX=-3.5 EndY=0 EndZ=0
    g6: ArcOfCircle CenterX=-3.5 CenterY=3 CenterZ=0 NormalX=0 NormalY=0 NormalZ=1 AngleXU=0 Radius=3 StartAngle=3.70042 EndAngle=4.71239
    g7: ArcOfCircle CenterX=0.739385 CenterY=5.65096 CenterZ=0 NormalX=0 NormalY=0 NormalZ=1 AngleXU=0 Radius=8 StartAngle=2.75061 EndAngle=3.70042
    g8: ArcOfCircle CenterX=-9.43052 CenterY=9.84299 CenterZ=0 NormalX=0 NormalY=0 NormalZ=1 AngleXU=0 Radius=3 StartAngle=5.89221 EndAngle=6.33555
    g9: LineSegment StartX=-6.43463 StartY=10 StartZ=0 EndX=-7.99315 EndY=39.7383 EndZ=0
  constraints (28):
    c: PointOnObject(g0,g-1)
    c: Vertical(g0)
    c: Coincident(g0,g1)
    c: PointOnObject(g1,g-2)
    c: Horizontal(g1)
    c: DistanceX(g1,g1) = 1.9
    c: DistanceY(g0,g0) = 35
    c: Distance(g2) = 10
    c: Coincident(g2,g1)
    c: PointOnObject(g2,g-2)
    c: Distance(g3) = 3
    c: Coincident(g3,g2)
    c: Horizontal(g3)
    c: Coincident(g5,g0)
    c: PointOnObject(g5,g-1)
    c: Tangent(g6,g5) = 1.5708
    c: Tangent(g7,g6) = -1.5708
    c: Tangent(g8,g7) = 1.5708
    c: Tangent(g9,g8) = -1.5708
    c: Tangent(g4,g3) = -1.5708
    c: Tangent(g9,g4) = 1.5708
    c: Angle(g-2,g9) = 0.0523599
    c: Radius(g4) = 5
    c: Radius(g6) = 3
    c: Radius(g7) = 8
    c: DistanceY(g8) = 10
    c: DistanceX(g5,g-1) = 3.5
    c: Radius(g8) = 3
FEATURE [PartDesign::Revolution] Revolution008
  Angle = 360
  Angle2 = 60
  Axis = (0,2e-16,1)
  Base = (0,0,0)
  Placement = pos=(0,0,0) rot=(1,0,0;1.5708rad)
  Profile = -> Sketch016
  ReferenceAxis = -> Sketch016 [V_Axis]
  Refine = true
  Suppressed = false
  Type = 0
FEATURE [Sketcher::SketchObject] Sketch017
  ArcFitTolerance = 1e-06
  AttachmentSupport = -> [Revolution008]
  FullyConstrained = true
  MakeInternals = false
  MapMode = 5
  Placement = pos=(0,1e-14,45) rot=(0,0,1;3.14159rad)
  sketch-geometry (14):
    g0: LineSegment [constr] StartX=-0.75 StartY=-2.65 StartZ=0 EndX=0.75 EndY=-2.65 EndZ=0
    g1: LineSegment [constr] StartX=0.75 StartY=-2.65 StartZ=0 EndX=0.75 EndY=2.65 EndZ=0
    g2: LineSegment [constr] StartX=0.75 StartY=2.65 StartZ=0 EndX=-0.75 EndY=2.65 EndZ=0
    g3: LineSegment [constr] StartX=-0.75 StartY=2.65 StartZ=0 EndX=-0.75 EndY=-2.65 EndZ=0
    g4: GeomPoint [constr] X=0 Y=0 Z=0
    g5: LineSegment StartX=-0.75 StartY=3.65 StartZ=0 EndX=0.75 EndY=3.65 EndZ=0
    g6: ArcOfCircle CenterX=5.625 CenterY=3.65 CenterZ=0 NormalX=0 NormalY=0 NormalZ=1 AngleXU=0 Radius=6.375 StartAngle=2.65164 EndAngle=3.14159
    g7: ArcOfCircle CenterX=-5.625 CenterY=3.65 CenterZ=0 NormalX=0 NormalY=0 NormalZ=1 AngleXU=0 Radius=6.375 StartAngle=0 EndAngle=0.489957
    g8: GeomPoint X=0.75 Y=0 Z=0
    g9: LineSegment StartX=-0.75 StartY=0.75 StartZ=0 EndX=-0.75 EndY=-0.75 EndZ=0
    g10: LineSegment StartX=-0.75 StartY=-0.75 StartZ=0 EndX=0.75 EndY=-0.75 EndZ=0
    g11: LineSegment StartX=0.75 StartY=-0.75 StartZ=0 EndX=0.75 EndY=0.75 EndZ=0
    g12: LineSegment StartX=0.75 StartY=0.75 StartZ=0 EndX=-0.75 EndY=0.75 EndZ=0
    g13: GeomPoint [constr] X=0 Y=0 Z=0
  constraints (37):
    c: Coincident(g0,g1)
    c: Coincident(g1,g2)
    c: Coincident(g2,g3)
    c: Coincident(g3,g0)
    c: Horizontal(g0)
    c: Horizontal(g2)
    c: Vertical(g1)
    c: Vertical(g3)
    c: Symmetric(g2,g0,g4)
    c: Distance(g1,g3) = 1.5
    c: Distance(g0,g2) = 5.3
    c: Coincident(g4,g-1)
    c: Horizontal(g5)
    c: Coincident(g6,g5)
    c: PointOnObject(g6,g-2)
    c: Coincident(g7,g6)
    c: Coincident(g7,g5)
    c: Equal(g7,g6)
    c: Equal(g2,g5)
    c: Vertical(g5,g2)
    c: DistanceY(g1,g5) = 1
    c: DistanceY(g5,g6) = 3
    c: Perpendicular(g7,g5)
    c: PointOnObject(g8,g1)
    c: PointOnObject(g8,g-1)
    c: Coincident(g9,g10)
    c: Coincident(g10,g11)
    c: Coincident(g11,g12)
    c: Coincident(g12,g9)
    c: Vertical(g9)
    c: Vertical(g11)
    c: Horizontal(g10)
    c: Horizontal(g12)
    c: Symmetric(g11,g9,g13)
    c: Coincident(g13,g4)
    c: PointOnObject(g10,g1)
    c: Equal(g11,g12)
FEATURE [PartDesign::Pocket] Pocket008
  BaseFeature = -> Revolution008
  Direction = (0,0,-1)
  Length = 2
  Length2 = 5
  Placement = pos=(0,0,0) rot=(1,0,0;1.5708rad)
  Profile = -> Sketch017
  ReferenceAxis = -> Sketch017 [N_Axis]
  Refine = true
  Suppressed = false
  Type = 0
FEATURE [PartDesign::Body] Body008
  AllowCompound = false
  Group = -> [Sketch016,Revolution008,Sketch017,Pocket008]
  Origin = -> Origin017
  Tip = -> Pocket008
COMPONENT P7 — recipe-attached ("10 - Half Round", modeled in this document).
Construction recipe (the document's own serialized feature program — sketch geometry with constraints, then the solid features built on it; lengths are millimeters unless a unit is written):

FEATURE [Sketcher::SketchObject] Sketch018
  ArcFitTolerance = 1e-06
  AttachmentSupport = -> [XZ_Plane019]
  FullyConstrained = true
  MakeInternals = false
  MapMode = 5
  Placement = pos=(0,0,0) rot=(1,0,0;1.5708rad)
  expr: Constraints[10] = <<Spreadsheet>>.TopFlatDiameter / 2
  expr: Constraints[22] = <<Spreadsheet>>.TopRadius
  expr: Constraints[23] = <<Spreadsheet>>.BottomRadius1
  expr: Constraints[24] = <<Spreadsheet>>.BottomRadius2
  expr: Constraints[25] = <<Spreadsheet>>.BottomToStraightHeight
  expr: Constraints[26] = <<Spreadsheet>>.BottomFlatDiameter / 2
  expr: Constraints[27] = <<Spreadsheet>>.BottomRadius3
  expr: Constraints[5] = <<Spreadsheet>>.HoleDiameter / 2
  expr: Constraints[6] = <<Spreadsheet>>.HoleDepth
  expr: Constraints[7] = <<Spreadsheet>>.TopSolidLength
  sketch-geometry (10):
    g0: LineSegment StartX=-1.9 StartY=0 StartZ=0 EndX=-1.9 EndY=35 EndZ=0
    g1: LineSegment StartX=-1.9 StartY=35 StartZ=0 EndX=0 EndY=35 EndZ=0
    g2: LineSegment StartX=0 StartY=35 StartZ=0 EndX=0 EndY=45 EndZ=0
    g3: LineSegment StartX=0 StartY=45 StartZ=0 EndX=-3 EndY=45 EndZ=0
    g4: ArcOfCircle CenterX=-3 CenterY=40 CenterZ=0 NormalX=0 NormalY=0 NormalZ=1 AngleXU=0 Radius=5 StartAngle=1.5708 EndAngle=3.19395
    g5: LineSegment StartX=-1.9 StartY=0 StartZ=0 EndX=-3.5 EndY=0 EndZ=0
    g6: ArcOfCircle CenterX=-3.5 CenterY=3 CenterZ=0 NormalX=0 NormalY=0 NormalZ=1 AngleXU=0 Radius=3 StartAngle=3.70042 EndAngle=4.71239
    g7: ArcOfCircle CenterX=0.739385 CenterY=5.65096 CenterZ=0 NormalX=0 NormalY=0 NormalZ=1 AngleXU=0 Radius=8 StartAngle=2.75061 EndAngle=3.70042
    g8: ArcOfCircle CenterX=-9.43052 CenterY=9.84299 CenterZ=0 NormalX=0 NormalY=0 NormalZ=1 AngleXU=0 Radius=3 StartAngle=5.89221 EndAngle=6.33555
    g9: LineSegment StartX=-6.43463 StartY=10 StartZ=0 EndX=-7.99315 EndY=39.7383 EndZ=0
  constraints (28):
    c: PointOnObject(g0,g-1)
    c: Vertical(g0)
    c: Coincident(g0,g1)
    c: PointOnObject(g1,g-2)
    c: Horizontal(g1)
    c: DistanceX(g1,g1) = 1.9
    c: DistanceY(g0,g0) = 35
    c: Distance(g2) = 10
    c: Coincident(g2,g1)
    c: PointOnObject(g2,g-2)
    c: Distance(g3) = 3
    c: Coincident(g3,g2)
    c: Horizontal(g3)
    c: Coincident(g5,g0)
    c: PointOnObject(g5,g-1)
    c: Tangent(g6,g5) = 1.5708
    c: Tangent(g7,g6) = -1.5708
    c: Tangent(g8,g7) = 1.5708
    c: Tangent(g9,g8) = -1.5708
    c: Tangent(g4,g3) = -1.5708
    c: Tangent(g9,g4) = 1.5708
    c: Angle(g-2,g9) = 0.0523599
    c: Radius(g4) = 5
    c: Radius(g6) = 3
    c: Radius(g7) = 8
    c: DistanceY(g8) = 10
    c: DistanceX(g5,g-1) = 3.5
    c: Radius(g8) = 3
FEATURE [PartDesign::Revolution] Revolution009
  Angle = 360
  Angle2 = 60
  Axis = (0,2e-16,1)
  Base = (0,0,0)
  Placement = pos=(0,0,0) rot=(1,0,0;1.5708rad)
  Profile = -> Sketch018
  ReferenceAxis = -> Sketch018 [V_Axis]
  Refine = true
  Suppressed = false
  Type = 0
FEATURE [Sketcher::SketchObject] Sketch019
  ArcFitTolerance = 1e-06
  AttachmentSupport = -> [Revolution009]
  FullyConstrained = true
  MakeInternals = false
  MapMode = 5
  Placement = pos=(0,1e-14,45) rot=(0,0,1;3.14159rad)
  sketch-geometry (12):
    g0: LineSegment [constr] StartX=-0.75 StartY=-2.65 StartZ=0 EndX=0.75 EndY=-2.65 EndZ=0
    g1: LineSegment [constr] StartX=0.75 StartY=-2.65 StartZ=0 EndX=0.75 EndY=2.65 EndZ=0
    g2: LineSegment [constr] StartX=0.75 StartY=2.65 StartZ=0 EndX=-0.75 EndY=2.65 EndZ=0
    g3: LineSegment [constr] StartX=-0.75 StartY=2.65 StartZ=0 EndX=-0.75 EndY=-2.65 EndZ=0
    g4: GeomPoint [constr] X=0 Y=0 Z=0
    g5: LineSegment StartX=-0.75 StartY=3.65 StartZ=0 EndX=0.75 EndY=3.65 EndZ=0
    g6: ArcOfCircle CenterX=5.625 CenterY=3.65 CenterZ=0 NormalX=0 NormalY=0 NormalZ=1 AngleXU=0 Radius=6.375 StartAngle=2.65164 EndAngle=3.14159
    g7: ArcOfCircle CenterX=-5.625 CenterY=3.65 CenterZ=0 NormalX=0 NormalY=0 NormalZ=1 AngleXU=0 Radius=6.375 StartAngle=0 EndAngle=0.489957
    g8: GeomPoint X=0.75 Y=0 Z=0
    g9: GeomPoint [constr] X=0 Y=0 Z=0
    g10: ArcOfCircle CenterX=-2.34083 CenterY=0 CenterZ=0 NormalX=0 NormalY=0 NormalZ=1 AngleXU=0 Radius=3.09083 StartAngle=5.25304 EndAngle=7.31333
    g11: LineSegment StartX=-0.75 StartY=-2.65 StartZ=0 EndX=-0.75 EndY=2.65 EndZ=0
  constraints (32):
    c: Coincident(g0,g1)
    c: Coincident(g1,g2)
    c: Coincident(g2,g3)
    c: Coincident(g3,g0)
    c: Horizontal(g0)
    c: Horizontal(g2)
    c: Vertical(g1)
    c: Vertical(g3)
    c: Symmetric(g2,g0,g4)
    c: Distance(g1,g3) = 1.5
    c: Distance(g0,g2) = 5.3
    c: Coincident(g4,g-1)
    c: Horizontal(g5)
    c: Coincident(g6,g5)
    c: PointOnObject(g6,g-2)
    c: Coincident(g7,g6)
    c: Coincident(g7,g5)
    c: Equal(g7,g6)
    c: Equal(g2,g5)
    c: Vertical(g5,g2)
    c: DistanceY(g1,g5) = 1
    c: DistanceY(g5,g6) = 3
    c: Perpendicular(g7,g5)
    c: PointOnObject(g8,g1)
    c: PointOnObject(g8,g-1)
    c: Coincident(g9,g4)
    c: PointOnObject(g10,g3)
    c: PointOnObject(g8,g10)
    c: PointOnObject(g10,g-1)
    c: Coincident(g11,g10)
    c: Coincident(g11,g10)
    c: Coincident(g10,g2)
FEATURE [PartDesign::Pocket] Pocket009
  BaseFeature = -> Revolution009
  Direction = (0,0,-1)
  Length = 2
  Length2 = 5
  Placement = pos=(0,0,0) rot=(1,0,0;1.5708rad)
  Profile = -> Sketch019
  ReferenceAxis = -> Sketch019 [N_Axis]
  Refine = true
  Suppressed = false
  Type = 0
FEATURE [PartDesign::Body] Body009
  AllowCompound = false
  Group = -> [Sketch018,Revolution009,Sketch019,Pocket009]
  Origin = -> Origin019
  Tip = -> Pocket009
COMPONENT P8 — recipe-attached ("1 - Flat Pointy", modeled in this document).
Construction recipe (the document's own serialized feature program — sketch geometry with constraints, then the solid features built on it; lengths are millimeters unless a unit is written):

FEATURE [Sketcher::SketchObject] Sketch020
  ArcFitTolerance = 1e-06
  AttachmentSupport = -> [XZ_Plane021]
  FullyConstrained = true
  MakeInternals = false
  MapMode = 5
  Placement = pos=(0,0,0) rot=(1,0,0;1.5708rad)
  expr: Constraints[10] = <<Spreadsheet>>.TopFlatDiameter / 2
  expr: Constraints[22] = <<Spreadsheet>>.TopRadius
  expr: Constraints[23] = <<Spreadsheet>>.BottomRadius1
  expr: Constraints[24] = <<Spreadsheet>>.BottomRadius2
  expr: Constraints[25] = <<Spreadsheet>>.BottomToStraightHeight
  expr: Constraints[26] = <<Spreadsheet>>.BottomFlatDiameter / 2
  expr: Constraints[27] = <<Spreadsheet>>.BottomRadius3
  expr: Constraints[5] = <<Spreadsheet>>.HoleDiameter / 2
  expr: Constraints[6] = <<Spreadsheet>>.HoleDepth
  expr: Constraints[7] = <<Spreadsheet>>.TopSolidLength
  sketch-geometry (10):
    g0: LineSegment StartX=-1.9 StartY=0 StartZ=0 EndX=-1.9 EndY=35 EndZ=0
    g1: LineSegment StartX=-1.9 StartY=35 StartZ=0 EndX=0 EndY=35 EndZ=0
    g2: LineSegment StartX=0 StartY=35 StartZ=0 EndX=0 EndY=45 EndZ=0
    g3: LineSegment StartX=0 StartY=45 StartZ=0 EndX=-3 EndY=45 EndZ=0
    g4: ArcOfCircle CenterX=-3 CenterY=40 CenterZ=0 NormalX=0 NormalY=0 NormalZ=1 AngleXU=0 Radius=5 StartAngle=1.5708 EndAngle=3.19395
    g5: LineSegment StartX=-1.9 StartY=0 StartZ=0 EndX=-3.5 EndY=0 EndZ=0
    g6: ArcOfCircle CenterX=-3.5 CenterY=3 CenterZ=0 NormalX=0 NormalY=0 NormalZ=1 AngleXU=0 Radius=3 StartAngle=3.70042 EndAngle=4.71239
    g7: ArcOfCircle CenterX=0.739385 CenterY=5.65096 CenterZ=0 NormalX=0 NormalY=0 NormalZ=1 AngleXU=0 Radius=8 StartAngle=2.75061 EndAngle=3.70042
    g8: ArcOfCircle CenterX=-9.43052 CenterY=9.84299 CenterZ=0 NormalX=0 NormalY=0 NormalZ=1 AngleXU=0 Radius=3 StartAngle=5.89221 EndAngle=6.33555
    g9: LineSegment StartX=-6.43463 StartY=10 StartZ=0 EndX=-7.99315 EndY=39.7383 EndZ=0
  constraints (28):
    c: PointOnObject(g0,g-1)
    c: Vertical(g0)
    c: Coincident(g0,g1)
    c: PointOnObject(g1,g-2)
    c: Horizontal(g1)
    c: DistanceX(g1,g1) = 1.9
    c: DistanceY(g0,g0) = 35
    c: Distance(g2) = 10
    c: Coincident(g2,g1)
    c: PointOnObject(g2,g-2)
    c: Distance(g3) = 3
    c: Coincident(g3,g2)
    c: Horizontal(g3)
    c: Coincident(g5,g0)
    c: PointOnObject(g5,g-1)
    c: Tangent(g6,g5) = 1.5708
    c: Tangent(g7,g6) = -1.5708
    c: Tangent(g8,g7) = 1.5708
    c: Tangent(g9,g8) = -1.5708
    c: Tangent(g4,g3) = -1.5708
    c: Tangent(g9,g4) = 1.5708
    c: Angle(g-2,g9) = 0.0523599
    c: Radius(g4) = 5
    c: Radius(g6) = 3
    c: Radius(g7) = 8
    c: DistanceY(g8) = 10
    c: DistanceX(g5,g-1) = 3.5
    c: Radius(g8) = 3
FEATURE [PartDesign::Revolution] Revolution010
  Angle = 360
  Angle2 = 60
  Axis = (0,2e-16,1)
  Base = (0,0,0)
  Placement = pos=(0,0,0) rot=(1,0,0;1.5708rad)
  Profile = -> Sketch020
  ReferenceAxis = -> Sketch020 [V_Axis]
  Refine = true
  Suppressed = false
  Type = 0
FEATURE [Sketcher::SketchObject] Sketch021
  ArcFitTolerance = 1e-06
  AttachmentSupport = -> [Revolution010]
  FullyConstrained = true
  MakeInternals = false
  MapMode = 5
  Placement = pos=(0,1e-14,45) rot=(0,0,1;3.14159rad)
  sketch-geometry (8):
    g0: LineSegment StartX=-0.75 StartY=-2.65 StartZ=0 EndX=0.75 EndY=-2.65 EndZ=0
    g1: LineSegment StartX=0.75 StartY=-2.65 StartZ=0 EndX=0.75 EndY=2.65 EndZ=0
    g2: LineSegment StartX=0.75 StartY=2.65 StartZ=0 EndX=-0.75 EndY=2.65 EndZ=0
    g3: LineSegment StartX=-0.75 StartY=2.65 StartZ=0 EndX=-0.75 EndY=-2.65 EndZ=0
    g4: GeomPoint [constr] X=0 Y=0 Z=0
    g5: LineSegment StartX=-0.75 StartY=3.65 StartZ=0 EndX=0.75 EndY=3.65 EndZ=0
    g6: ArcOfCircle CenterX=5.625 CenterY=3.65 CenterZ=0 NormalX=0 NormalY=0 NormalZ=1 AngleXU=0 Radius=6.375 StartAngle=2.65164 EndAngle=3.14159
    g7: ArcOfCircle CenterX=-5.625 CenterY=3.65 CenterZ=0 NormalX=0 NormalY=0 NormalZ=1 AngleXU=0 Radius=6.375 StartAngle=0 EndAngle=0.489957
  constraints (23):
    c: Coincident(g0,g1)
    c: Coincident(g1,g2)
    c: Coincident(g2,g3)
    c: Coincident(g3,g0)
    c: Horizontal(g0)
    c: Horizontal(g2)
    c: Vertical(g1)
    c: Vertical(g3)
    c: Symmetric(g2,g0,g4)
    c: Distance(g1,g3) = 1.5
    c: Distance(g0,g2) = 5.3
    c: Coincident(g4,g-1)
    c: Horizontal(g5)
    c: Coincident(g6,g5)
    c: PointOnObject(g6,g-2)
    c: Coincident(g7,g6)
    c: Coincident(g7,g5)
    c: Equal(g7,g6)
    c: Equal(g2,g5)
    c: Vertical(g5,g2)
    c: DistanceY(g1,g5) = 1
    c: DistanceY(g5,g6) = 3
    c: Perpendicular(g7,g5)
FEATURE [PartDesign::Pocket] Pocket010
  BaseFeature = -> Revolution010
  Direction = (0,0,-1)
  Length = 2
  Length2 = 5
  Placement = pos=(0,0,0) rot=(1,0,0;1.5708rad)
  Profile = -> Sketch021
  ReferenceAxis = -> Sketch021 [N_Axis]
  Refine = true
  Suppressed = false
  Type = 0
FEATURE [PartDesign::Body] Body010
  AllowCompound = false
  Group = -> [Sketch020,Revolution010,Sketch021,Pocket010]
  Origin = -> Origin021
  Tip = -> Pocket010
COMPONENT P9 — recipe-attached ("2 - Flat Straight", modeled in this document).
Construction recipe (the document's own serialized feature program — sketch geometry with constraints, then the solid features built on it; lengths are millimeters unless a unit is written):

FEATURE [Sketcher::SketchObject] Sketch022
  ArcFitTolerance = 1e-06
  AttachmentSupport = -> [XZ_Plane023]
  FullyConstrained = true
  MakeInternals = false
  MapMode = 5
  Placement = pos=(0,0,0) rot=(1,0,0;1.5708rad)
  expr: Constraints[10] = <<Spreadsheet>>.TopFlatDiameter / 2
  expr: Constraints[22] = <<Spreadsheet>>.TopRadius
  expr: Constraints[23] = <<Spreadsheet>>.BottomRadius1
  expr: Constraints[24] = <<Spreadsheet>>.BottomRadius2
  expr: Constraints[25] = <<Spreadsheet>>.BottomToStraightHeight
  expr: Constraints[26] = <<Spreadsheet>>.BottomFlatDiameter / 2
  expr: Constraints[27] = <<Spreadsheet>>.BottomRadius3
  expr: Constraints[5] = <<Spreadsheet>>.HoleDiameter / 2
  expr: Constraints[6] = <<Spreadsheet>>.HoleDepth
  expr: Constraints[7] = <<Spreadsheet>>.TopSolidLength
  sketch-geometry (10):
    g0: LineSegment StartX=-1.9 StartY=0 StartZ=0 EndX=-1.9 EndY=35 EndZ=0
    g1: LineSegment StartX=-1.9 StartY=35 StartZ=0 EndX=0 EndY=35 EndZ=0
    g2: LineSegment StartX=0 StartY=35 StartZ=0 EndX=0 EndY=45 EndZ=0
    g3: LineSegment StartX=0 StartY=45 StartZ=0 EndX=-3 EndY=45 EndZ=0
    g4: ArcOfCircle CenterX=-3 CenterY=40 CenterZ=0 NormalX=0 NormalY=0 NormalZ=1 AngleXU=0 Radius=5 StartAngle=1.5708 EndAngle=3.19395
    g5: LineSegment StartX=-1.9 StartY=0 StartZ=0 EndX=-3.5 EndY=0 EndZ=0
    g6: ArcOfCircle CenterX=-3.5 CenterY=3 CenterZ=0 NormalX=0 NormalY=0 NormalZ=1 AngleXU=0 Radius=3 StartAngle=3.70042 EndAngle=4.71239
    g7: ArcOfCircle CenterX=0.739385 CenterY=5.65096 CenterZ=0 NormalX=0 NormalY=0 NormalZ=1 AngleXU=0 Radius=8 StartAngle=2.75061 EndAngle=3.70042
    g8: ArcOfCircle CenterX=-9.43052 CenterY=9.84299 CenterZ=0 NormalX=0 NormalY=0 NormalZ=1 AngleXU=0 Radius=3 StartAngle=5.89221 EndAngle=6.33555
    g9: LineSegment StartX=-6.43463 StartY=10 StartZ=0 EndX=-7.99315 EndY=39.7383 EndZ=0
  constraints (28):
    c: PointOnObject(g0,g-1)
    c: Vertical(g0)
    c: Coincident(g0,g1)
    c: PointOnObject(g1,g-2)
    c: Horizontal(g1)
    c: DistanceX(g1,g1) = 1.9
    c: DistanceY(g0,g0) = 35
    c: Distance(g2) = 10
    c: Coincident(g2,g1)
    c: PointOnObject(g2,g-2)
    c: Distance(g3) = 3
    c: Coincident(g3,g2)
    c: Horizontal(g3)
    c: Coincident(g5,g0)
    c: PointOnObject(g5,g-1)
    c: Tangent(g6,g5) = 1.5708
    c: Tangent(g7,g6) = -1.5708
    c: Tangent(g8,g7) = 1.5708
    c: Tangent(g9,g8) = -1.5708
    c: Tangent(g4,g3) = -1.5708
    c: Tangent(g9,g4) = 1.5708
    c: Angle(g-2,g9) = 0.0523599
    c: Radius(g4) = 5
    c: Radius(g6) = 3
    c: Radius(g7) = 8
    c: DistanceY(g8) = 10
    c: DistanceX(g5,g-1) = 3.5
    c: Radius(g8) = 3
FEATURE [PartDesign::Revolution] Revolution011
  Angle = 360
  Angle2 = 60
  Axis = (0,2e-16,1)
  Base = (0,0,0)
  Placement = pos=(0,0,0) rot=(1,0,0;1.5708rad)
  Profile = -> Sketch022
  ReferenceAxis = -> Sketch022 [V_Axis]
  Refine = true
  Suppressed = false
  Type = 0
FEATURE [Sketcher::SketchObject] Sketch023
  ArcFitTolerance = 1e-06
  AttachmentSupport = -> [Revolution011]
  FullyConstrained = true
  MakeInternals = false
  MapMode = 5
  Placement = pos=(0,1e-14,45) rot=(0,0,1;3.14159rad)
  sketch-geometry (9):
    g0: LineSegment StartX=-0.75 StartY=-2.65 StartZ=0 EndX=0.75 EndY=-2.65 EndZ=0
    g1: LineSegment StartX=0.75 StartY=-2.65 StartZ=0 EndX=0.75 EndY=2.65 EndZ=0
    g2: LineSegment StartX=0.75 StartY=2.65 StartZ=0 EndX=-0.75 EndY=2.65 EndZ=0
    g3: LineSegment StartX=-0.75 StartY=2.65 StartZ=0 EndX=-0.75 EndY=-2.65 EndZ=0
    g4: GeomPoint [constr] X=0 Y=0 Z=0
    g5: LineSegment StartX=-0.75 StartY=3.65 StartZ=0 EndX=0.75 EndY=3.65 EndZ=0
    g6: LineSegment StartX=-0.75 StartY=3.65 StartZ=0 EndX=-0.75 EndY=6.65 EndZ=0
    g7: LineSegment StartX=-0.75 StartY=6.65 StartZ=0 EndX=0.75 EndY=6.65 EndZ=0
    g8: LineSegment StartX=0.75 StartY=6.65 StartZ=0 EndX=0.75 EndY=3.65 EndZ=0
  constraints (24):
    c: Coincident(g0,g1)
    c: Coincident(g1,g2)
    c: Coincident(g2,g3)
    c: Coincident(g3,g0)
    c: Horizontal(g0)
    c: Horizontal(g2)
    c: Vertical(g1)
    c: Vertical(g3)
    c: Symmetric(g2,g0,g4)
    c: Distance(g1,g3) = 1.5
    c: Distance(g0,g2) = 5.3
    c: Coincident(g4,g-1)
    c: Horizontal(g5)
    c: Equal(g2,g5)
    c: Vertical(g5,g2)
    c: DistanceY(g1,g5) = 1
    c: Coincident(g5,g6)
    c: Vertical(g6)
    c: Coincident(g6,g7)
    c: Horizontal(g7)
    c: Coincident(g7,g8)
    c: Coincident(g8,g5)
    c: Vertical(g8)
    c: DistanceY(g6,g6) = 3
FEATURE [PartDesign::Pocket] Pocket011
  BaseFeature = -> Revolution011
  Direction = (0,0,-1)
  Length = 2
  Length2 = 5
  Placement = pos=(0,0,0) rot=(1,0,0;1.5708rad)
  Profile = -> Sketch023
  ReferenceAxis = -> Sketch023 [N_Axis]
  Refine = true
  Suppressed = false
  Type = 0
FEATURE [PartDesign::Body] Body011
  AllowCompound = false
  Group = -> [Sketch022,Revolution011,Sketch023,Pocket011]
  Origin = -> Origin023
  Tip = -> Pocket011
PROVENANCE & LICENSES
A FreeCAD (.FCStd) document from a public repository crawl; recipes are the document's own serialized feature recipes (and, for linked parts, companion documents' recipes).
License: as declared in the source repository (recorded in the dataset sidecar).
